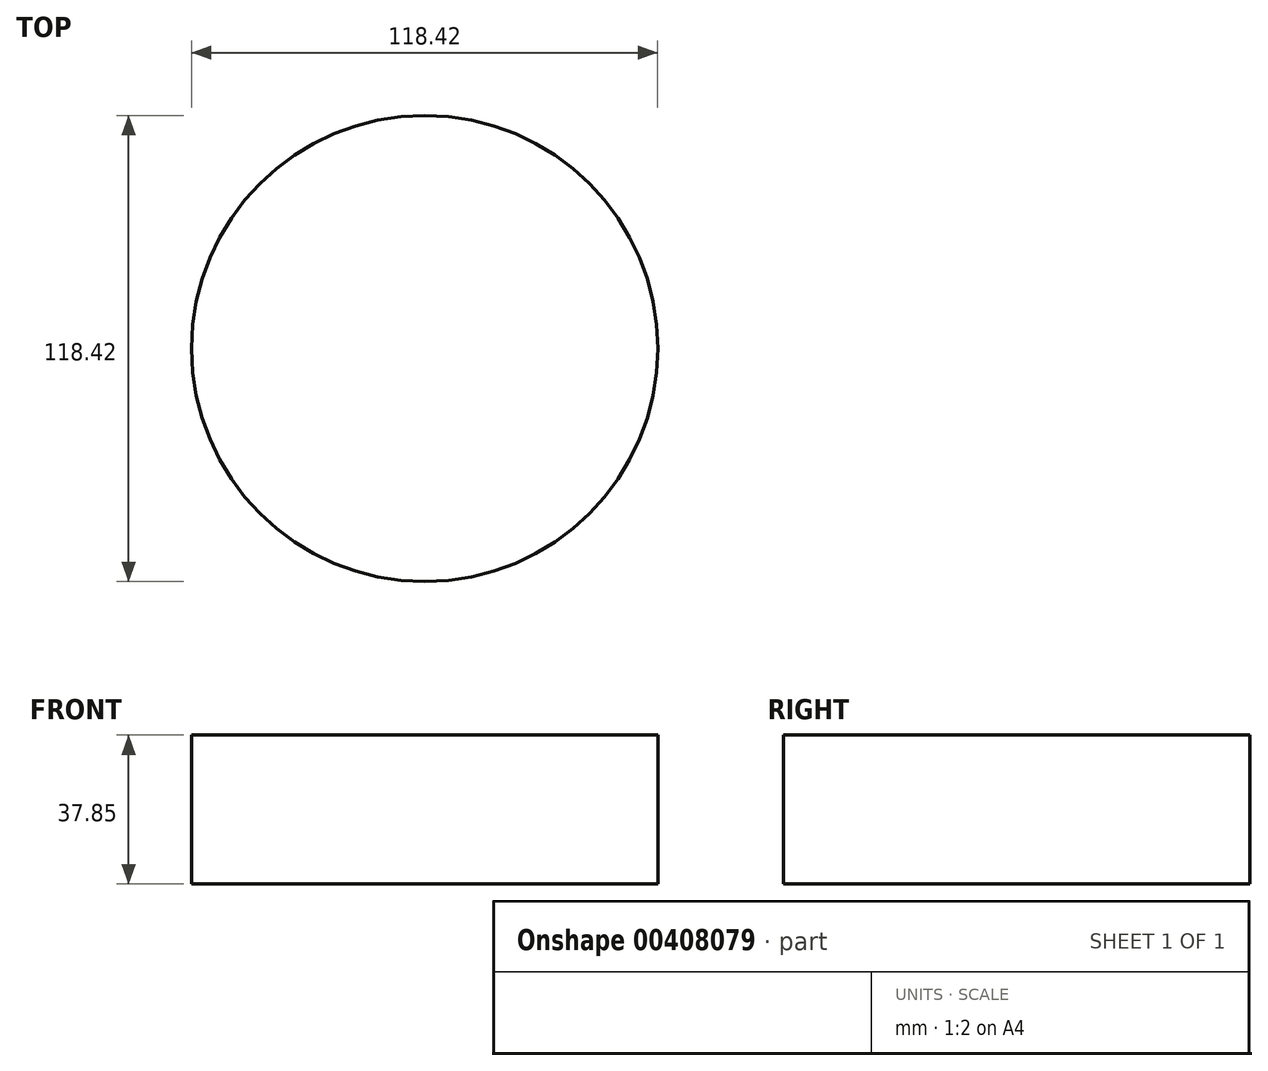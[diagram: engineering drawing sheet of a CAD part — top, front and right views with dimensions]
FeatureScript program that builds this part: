
annotation { "Feature Type Name" : "Feature", "Feature Type Description" : "" }
export const myFeature = defineFeature(function(context is Context, id is Id, definition is map)
    precondition{}
    {
        {
            var Q0;
            Q0=qCreatedBy(makeId("Top.planeOp"),FACE);
            var sketch = newSketch(context, id + "F0", { "sketchPlane" : qUnion([Q0])});
            skCircle(sketch, "E0", {"center": v(0, 0) * mm, "radius": 59.21 * mm});
            skSolve(sketch);
        }
        {
            var Q0;
            Q0=makeQuery(id+"F0.imprint","IMPRINT",FACE,{"disambiguationData":[TD([[makeQuery(id+"F0.imprint","IMPRINT",EDGE,{"derivedFrom":sQuery(id+"F0.wireOp",EDGE,"E0")}),1.0]])]});
            extrude(context, id + "F1", {"entities" : qUnion([Q0]), "depth" : 37.85 * mm});
        }
    });
